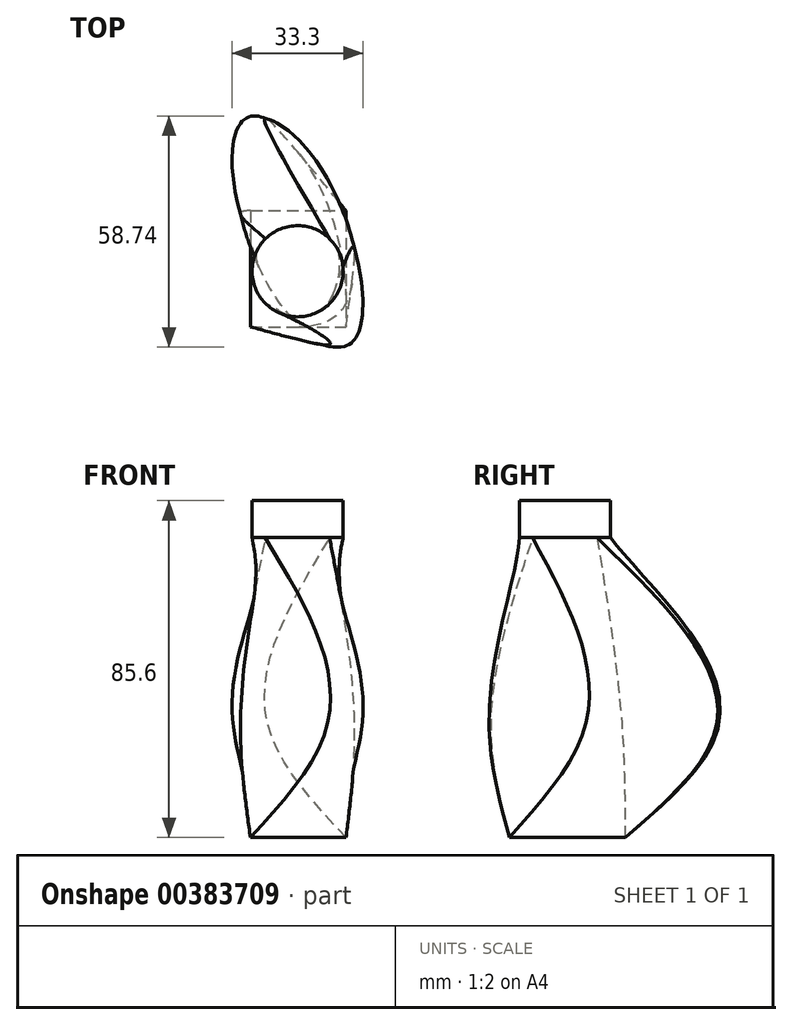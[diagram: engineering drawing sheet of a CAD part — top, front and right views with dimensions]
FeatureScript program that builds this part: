
annotation { "Feature Type Name" : "Feature", "Feature Type Description" : "" }
export const myFeature = defineFeature(function(context is Context, id is Id, definition is map)
    precondition{}
    {
        {
            var Q0;
            Q0=qCreatedBy(makeId("Top.planeOp"),FACE);
            var sketch = newSketch(context, id + "F0", { "sketchPlane" : qUnion([Q0])});
            skLineSegment(sketch, "E0.bottom", {"start": v(-11.97, 15.4) * mm, "end": v(12.29, 15.4) * mm});
            skLineSegment(sketch, "E0.top", {"start": v(-11.97, -14.15) * mm, "end": v(12.29, -14.15) * mm});
            skLineSegment(sketch, "E0.left", {"start": v(-11.97, 15.4) * mm, "end": v(-11.97, -14.15) * mm});
            skLineSegment(sketch, "E0.right", {"start": v(12.29, 15.4) * mm, "end": v(12.29, -14.15) * mm});
            skSolve(sketch);
        }
        {
            var Q0;
            Q0=qCreatedBy(makeId("Top.planeOp"),FACE);
            cPlane(context, id + "F1", {"entities" : qUnion([Q0]), "cplaneType" : CPlaneType.OFFSET, "offset" : 25.4 * mm, "width" : 152.4 * mm, "height" : 152.4 * mm});
        }
        {
            var Q0;
            Q0=qCreatedBy(id+"F1.planeOp",FACE);
            var sketch = newSketch(context, id + "F2", { "sketchPlane" : qUnion([Q0])});
            skEllipse(sketch, "E1", {"center": v(0, 9.49) * mm, "majorRadius": 30.38 * mm, "minorRadius": 12.3 * mm, "majorAxis": v(-0.36, 0.93)});
            skSolve(sketch);
        }
        {
            var Q0;
            Q0=qCreatedBy(id+"F1.planeOp",FACE);
            cPlane(context, id + "F3", {"entities" : qUnion([Q0]), "cplaneType" : CPlaneType.OFFSET, "offset" : 25.4 * mm, "width" : 152.4 * mm, "height" : 152.4 * mm});
        }
        {
            var Q0;
            Q0=qCreatedBy(id+"F3.planeOp",FACE);
            cPlane(context, id + "F4", {"entities" : qUnion([Q0]), "cplaneType" : CPlaneType.OFFSET, "offset" : 25.4 * mm, "width" : 152.4 * mm, "height" : 152.4 * mm});
        }
        {
            var Q0;
            Q0=qCreatedBy(id+"F4.planeOp",FACE);
            var sketch = newSketch(context, id + "F5", { "sketchPlane" : qUnion([Q0])});
            skCircle(sketch, "E2", {"center": v(0, 0) * mm, "radius": 11.58 * mm});
            skSolve(sketch);
        }
        {
            var Q0;
            Q0=makeQuery(id+"F0.imprint","IMPRINT",FACE,{"disambiguationData":[TD([[makeQuery(id+"F0.imprint","IMPRINT",EDGE,{"derivedFrom":sQuery(id+"F0.wireOp",EDGE,"E0.bottom")}),-1.0]])]});
            var Q1;
            Q1=makeQuery(id+"F2.imprint","IMPRINT",FACE,{"disambiguationData":[TD([[makeQuery(id+"F2.imprint","IMPRINT",EDGE,{"derivedFrom":sQuery(id+"F2.wireOp",EDGE,"E1")}),1.0]])]});
            var Q2;
            Q2=makeQuery(id+"F5.imprint","IMPRINT",FACE,{"disambiguationData":[TD([[makeQuery(id+"F5.imprint","IMPRINT",EDGE,{"derivedFrom":sQuery(id+"F5.wireOp",EDGE,"E2")}),1.0]])]});
            loft(context, id + "F6", {"sheetProfilesArray" : [{ "sheetProfileEntities" : qUnion([Q0]) }, { "sheetProfileEntities" : qUnion([Q1]) }, { "sheetProfileEntities" : qUnion([Q2]) }]});
        }
        {
            var Q0;
            Q0=makeQuery(id+"F6.opLoft","CAP_FACE",FACE,{"disambiguationData":[OSD([makeQuery(id+"F5.imprint","IMPRINT",FACE,{"disambiguationData":[TD([[makeQuery(id+"F5.imprint","IMPRINT",EDGE,{"derivedFrom":sQuery(id+"F5.wireOp",EDGE,"E2")}),1.0]])]})])],"isStart":true});
            extrude(context, id + "F7", {"entities" : qUnion([Q0]), "operationType" : NewBodyOperationType.ADD, "depth" : 9.4 * mm});
        }
    });
